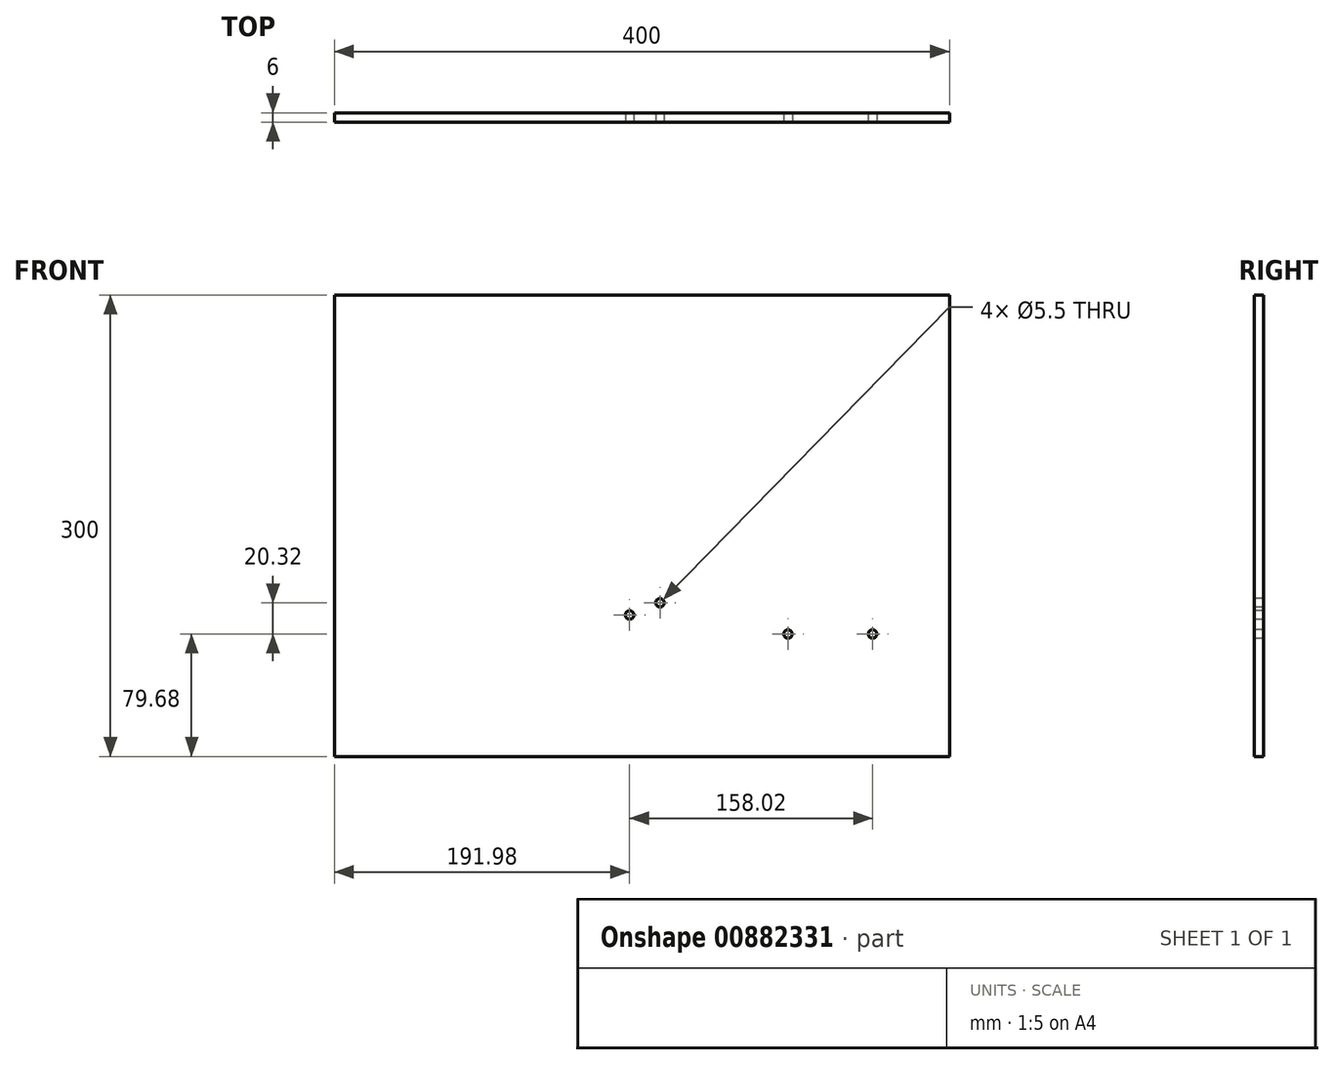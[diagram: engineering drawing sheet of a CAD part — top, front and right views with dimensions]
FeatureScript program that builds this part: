
annotation { "Feature Type Name" : "Feature", "Feature Type Description" : "" }
export const myFeature = defineFeature(function(context is Context, id is Id, definition is map)
    precondition{}
    {
        {
            var Q0;
            Q0=qCreatedBy(makeId("Front.planeOp"),FACE);
            var sketch = newSketch(context, id + "F0", { "sketchPlane" : qUnion([Q0])});
            skLineSegment(sketch, "E0.bottom", {"start": v(200, 150) * mm, "end": v(-200, 150) * mm});
            skLineSegment(sketch, "E0.top", {"start": v(200, -150) * mm, "end": v(-200, -150) * mm});
            skLineSegment(sketch, "E0.left", {"start": v(200, 150) * mm, "end": v(200, -150) * mm});
            skLineSegment(sketch, "E0.right", {"start": v(-200, 150) * mm, "end": v(-200, -150) * mm});
            skPoint(sketch, "E0.middle", {"position": v(0, 0) * mm});
            skSolve(sketch);
        }
        {
            var Q0;
            Q0=makeQuery(id+"F0.imprint","IMPRINT",FACE,{"disambiguationData":[TD([[makeQuery(id+"F0.imprint","IMPRINT",EDGE,{"derivedFrom":sQuery(id+"F0.wireOp",EDGE,"E0.bottom")}),1.0]])]});
            extrude(context, id + "F1", {"entities" : qUnion([Q0]), "oppositeDirection" : true, "depth" : 6 * mm, "offsetDistance" : 25 * mm});
        }
        {
            var Q0;
            Q0=makeQuery(id+"F1.opExtrude","CAP_FACE",FACE,{"disambiguationData":[OSD([sQuery(id+"F0.wireOp",EDGE,"E0.bottom"),sQuery(id+"F0.wireOp",EDGE,"E0.top"),sQuery(id+"F0.wireOp",EDGE,"E0.left"),sQuery(id+"F0.wireOp",EDGE,"E0.right")])],"isStart":true});
            var sketch = newSketch(context, id + "F2", { "sketchPlane" : qUnion([Q0])});
            skLineSegment(sketch, "E1", {"start": v(-200, 75) * mm, "end": v(200, 75) * mm});
            skLineSegment(sketch, "E2", {"start": v(-200, -50) * mm, "end": v(200, -50) * mm});
            skPoint(sketch, "E3", {"position": v(11.75, -50) * mm});
            skPoint(sketch, "E4", {"position": v(0, 75) * mm});
            skPoint(sketch, "E5", {"position": v(-122.98, -50) * mm});
            skPoint(sketch, "E6", {"position": v(150, -70.32) * mm});
            skSolve(sketch);
        }
        {
            var Q0;
            {var subQ0=sQuery(id+"F2.wireOp",EDGE,"E1");Q0=makeQuery(id+"F2.imprint","IMPRINT",FACE,{"disambiguationData":[TD([[makeQuery(id+"F2.imprint","IMPRINT",EDGE,{"derivedFrom":subQ0}),-1.0]])]});}
            var sketch = newSketch(context, id + "F3", { "sketchPlane" : qUnion([Q0])});
            skCircle(sketch, "E7", {"center": v(150, -70.32) * mm, "radius": 2.75 * mm});
            skCircle(sketch, "E8", {"center": v(95, -70.32) * mm, "radius": 2.75 * mm});
            skCircle(sketch, "E9", {"center": v(11.75, -50) * mm, "radius": 2.75 * mm});
            skCircle(sketch, "E10", {"center": v(-8.02, -57.96) * mm, "radius": 2.75 * mm});
            skSolve(sketch);
        }
        {
            var Q0;
            Q0 = qSketchRegion(id + "F3", true);
            extrude(context, id + "F4", {"entities" : qUnion([Q0]), "operationType" : NewBodyOperationType.REMOVE, "endBound" : BoundingType.UP_TO_NEXT, "oppositeDirection" : true, "depth" : 25 * mm, "offsetDistance" : 25 * mm});
        }
    });
